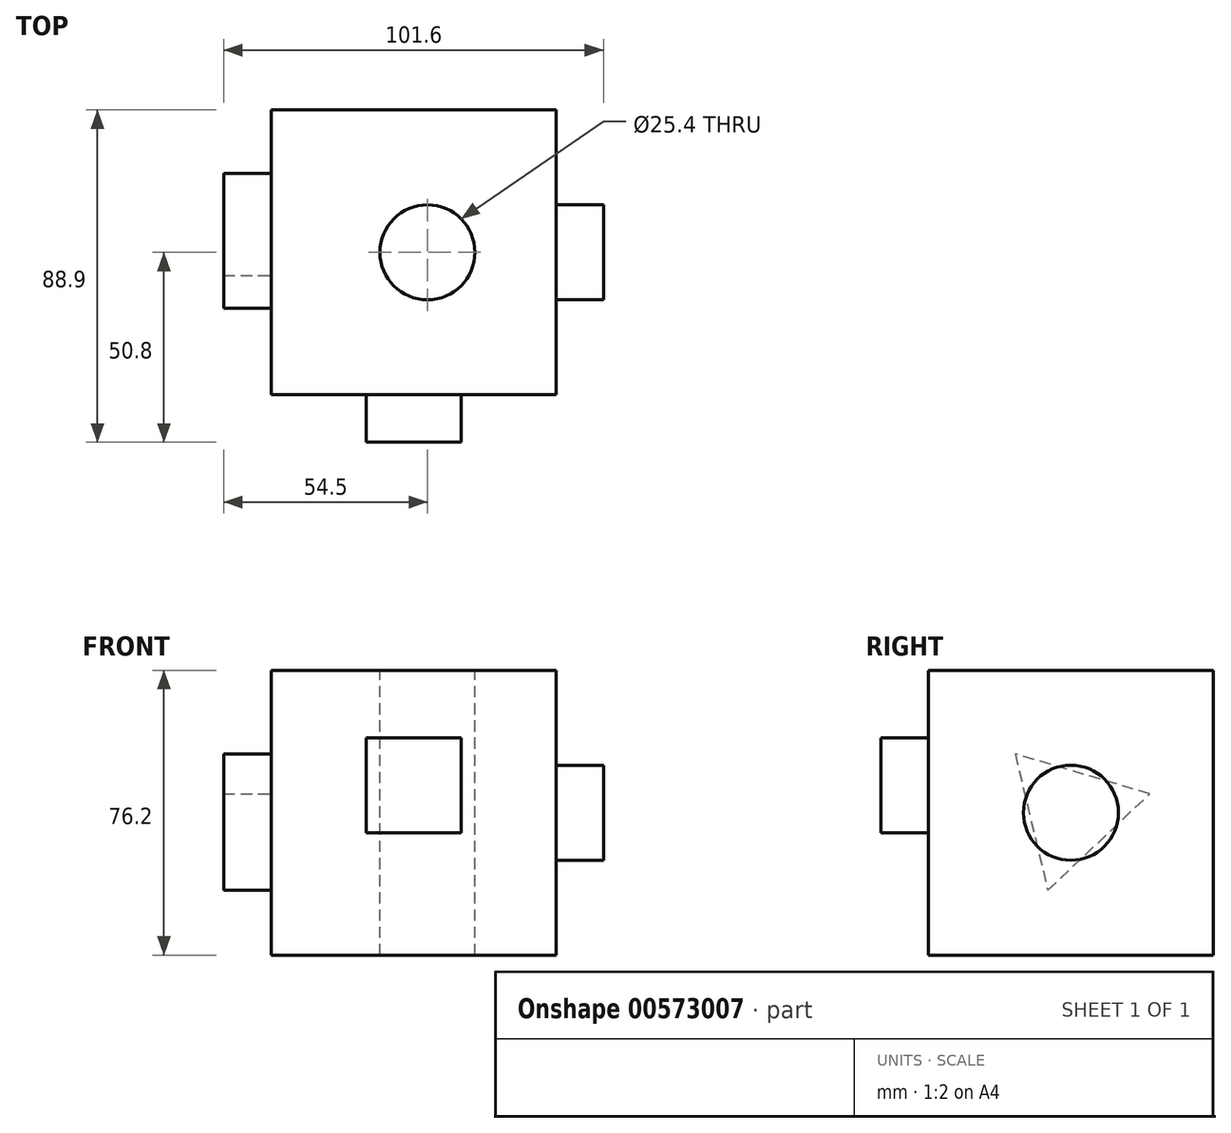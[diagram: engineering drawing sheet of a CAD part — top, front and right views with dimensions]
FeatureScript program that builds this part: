
annotation { "Feature Type Name" : "Feature", "Feature Type Description" : "" }
export const myFeature = defineFeature(function(context is Context, id is Id, definition is map)
    precondition{}
    {
        {
            var Q0;
            Q0=qCreatedBy(makeId("Front.planeOp"),FACE);
            var sketch = newSketch(context, id + "F0", { "sketchPlane" : qUnion([Q0])});
            skLineSegment(sketch, "E0.bottom", {"start": v(-41.8, -43.41) * mm, "end": v(34.4, -43.41) * mm});
            skLineSegment(sketch, "E0.top", {"start": v(-41.8, 32.79) * mm, "end": v(34.4, 32.79) * mm});
            skLineSegment(sketch, "E0.left", {"start": v(-41.8, -43.41) * mm, "end": v(-41.8, 32.79) * mm});
            skLineSegment(sketch, "E0.right", {"start": v(34.4, -43.41) * mm, "end": v(34.4, 32.79) * mm});
            skSolve(sketch);
        }
        {
            var Q0;
            Q0=makeQuery(id+"F0.imprint","IMPRINT",FACE,{"disambiguationData":[TD([[makeQuery(id+"F0.imprint","IMPRINT",EDGE,{"derivedFrom":sQuery(id+"F0.wireOp",EDGE,"E0.bottom")}),1.0]])]});
            extrude(context, id + "F1", {"entities" : qUnion([Q0]), "oppositeDirection" : true, "depth" : 76.2 * mm, "offsetDistance" : 25.4 * mm});
        }
        {
            var Q0;
            Q0=makeQuery(id+"F1.opExtrude","CAP_FACE",FACE,{"disambiguationData":[OSD([sQuery(id+"F0.wireOp",EDGE,"E0.bottom"),sQuery(id+"F0.wireOp",EDGE,"E0.top"),sQuery(id+"F0.wireOp",EDGE,"E0.left"),sQuery(id+"F0.wireOp",EDGE,"E0.right")])],"isStart":true});
            var sketch = newSketch(context, id + "F2", { "sketchPlane" : qUnion([Q0])});
            skLineSegment(sketch, "E1.bottom", {"start": v(-16.4, 14.66) * mm, "end": v(9, 14.66) * mm});
            skLineSegment(sketch, "E1.top", {"start": v(-16.4, -10.74) * mm, "end": v(9, -10.74) * mm});
            skLineSegment(sketch, "E1.left", {"start": v(-16.4, 14.66) * mm, "end": v(-16.4, -10.74) * mm});
            skLineSegment(sketch, "E1.right", {"start": v(9, 14.66) * mm, "end": v(9, -10.74) * mm});
            skSolve(sketch);
        }
        {
            var Q0;
            Q0 = qSketchRegion(id + "F2", true);
            extrude(context, id + "F3", {"entities" : qUnion([Q0]), "operationType" : NewBodyOperationType.ADD, "depth" : 12.7 * mm, "offsetDistance" : 25.4 * mm});
        }
        {
            var Q0;
            Q0=makeQuery(id+"F1.opExtrude","SWEPT_FACE",FACE,{"disambiguationData":[OSD([sQuery(id+"F0.wireOp",EDGE,"E0.right")])]});
            var sketch = newSketch(context, id + "F4", { "sketchPlane" : qUnion([Q0])});
            skCircle(sketch, "E2", {"center": v(38.1, -5.31) * mm, "radius": 12.7 * mm});
            skSolve(sketch);
        }
        {
            var Q0;
            Q0=makeQuery(id+"F4.imprint","IMPRINT",FACE,{"disambiguationData":[TD([[makeQuery(id+"F4.imprint","IMPRINT",EDGE,{"derivedFrom":sQuery(id+"F4.wireOp",EDGE,"E2")}),1.0]])]});
            extrude(context, id + "F5", {"entities" : qUnion([Q0]), "operationType" : NewBodyOperationType.ADD, "depth" : 12.7 * mm, "offsetDistance" : 25.4 * mm});
        }
        {
            var Q0;
            Q0=makeQuery(id+"F1.opExtrude","SWEPT_FACE",FACE,{"disambiguationData":[OSD([sQuery(id+"F0.wireOp",EDGE,"E0.top")])]});
            var sketch = newSketch(context, id + "F6", { "sketchPlane" : qUnion([Q0])});
            skPoint(sketch, "E3", {"position": v(0, 38.1) * mm});
            skSolve(sketch);
        }
        {
            var Q0;
            Q0=sQuery(id+"F6.wireOp",VERTEX,"E3");
            var Q1;
            Q1=makeQuery(id+"F1.opExtrude","SWEPT_BODY",BODY,{"disambiguationData":[OSD([sQuery(id+"F0.wireOp",EDGE,"E0.bottom"),sQuery(id+"F0.wireOp",EDGE,"E0.top"),sQuery(id+"F0.wireOp",EDGE,"E0.left"),sQuery(id+"F0.wireOp",EDGE,"E0.right")])]});
            hole(context, id + "F7", {"style" : HoleStyle.SIMPLE, "endStyle" : HoleEndStyle.THROUGH, "holeDiameter" : 25.4 * mm, "isTappedThrough" : true, "tappedDepth" : 12.7 * mm, "tapClearance" : 3, "locations" : qUnion([Q0]), "scope" : qUnion([Q1])});
        }
        {
            var Q0;
            Q0=makeQuery(id+"F1.opExtrude","SWEPT_FACE",FACE,{"disambiguationData":[OSD([sQuery(id+"F0.wireOp",EDGE,"E0.left")])]});
            var sketch = newSketch(context, id + "F8", { "sketchPlane" : qUnion([Q0])});
            skCircle(sketch, "E4.cCircle", {"center": v(-38.1, -5.31) * mm, "radius": 10.84 * mm, "construction": true});
            skLineSegment(sketch, "E4.0", {"start": v(-31.93, -26.1) * mm, "end": v(-59.18, -0.26) * mm});
            skLineSegment(sketch, "E4.1", {"start": v(-59.18, -0.26) * mm, "end": v(-23.18, 10.42) * mm});
            skLineSegment(sketch, "E4.2", {"start": v(-23.18, 10.42) * mm, "end": v(-31.93, -26.1) * mm});
            skPoint(sketch, "E4.0.midPoint", {"position": v(-45.56, -13.18) * mm});
            skSolve(sketch);
        }
        {
            var Q0;
            Q0=makeQuery(id+"F8.imprint","IMPRINT",FACE,{"disambiguationData":[TD([[makeQuery(id+"F8.imprint","IMPRINT",EDGE,{"derivedFrom":sQuery(id+"F8.wireOp",EDGE,"E4.0")}),-1.0]])]});
            extrude(context, id + "F9", {"entities" : qUnion([Q0]), "operationType" : NewBodyOperationType.ADD, "depth" : 12.7 * mm, "offsetDistance" : 25.4 * mm});
        }
    });
